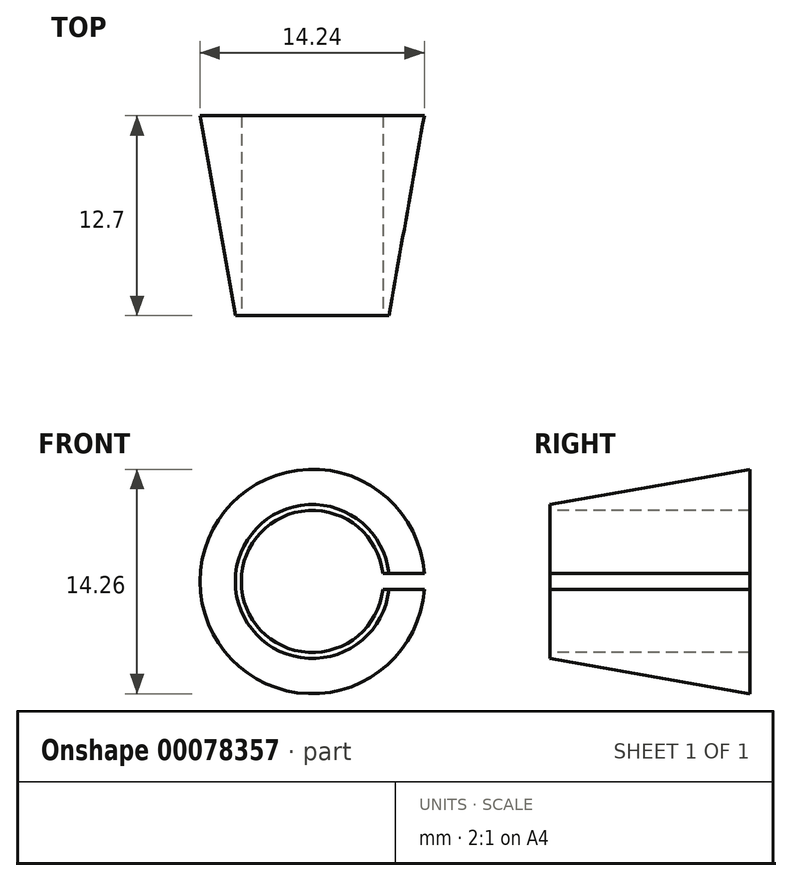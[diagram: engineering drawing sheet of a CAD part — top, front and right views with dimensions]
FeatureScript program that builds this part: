
annotation { "Feature Type Name" : "Feature", "Feature Type Description" : "" }
export const myFeature = defineFeature(function(context is Context, id is Id, definition is map)
    precondition{}
    {
        {
            var Q0;
            Q0=qCreatedBy(makeId("Right.planeOp"),FACE);
            var sketch = newSketch(context, id + "F0", { "sketchPlane" : qUnion([Q0])});
            skLineSegment(sketch, "E0", {"start": v(0, 4.89) * mm, "end": v(12.7, 7.13) * mm});
            skLineSegment(sketch, "E1", {"start": v(0, 0) * mm, "end": v(12.7, 0) * mm, "construction": true});
            skLineSegment(sketch, "E2", {"start": v(0, 4.5) * mm, "end": v(0, 4.89) * mm});
            skLineSegment(sketch, "E3", {"start": v(0, 4.5) * mm, "end": v(12.7, 4.5) * mm});
            skLineSegment(sketch, "E4", {"start": v(12.7, 7.13) * mm, "end": v(12.7, 4.5) * mm});
            skSolve(sketch);
        }
        {
            var Q0;
            Q0=makeQuery(id+"F0.imprint","IMPRINT",FACE,{"disambiguationData":[TD([[makeQuery(id+"F0.imprint","IMPRINT",EDGE,{"derivedFrom":sQuery(id+"F0.wireOp",EDGE,"E0")}),-1.0]])]});
            var Q1;
            Q1=sQuery(id+"F0.wireOp",EDGE,"E1");
            var Q2;
            Q2=sQuery(id+"F0.wireOp",EDGE,"E1");
            revolve(context, id + "F1", {"entities" : qUnion([Q0]), "surfaceEntities" : qUnion([Q1]), "axis" : qUnion([Q2]), "revolveType" : RevolveType.FULL});
        }
        {
            var Q0;
            Q0=qCreatedBy(makeId("Top.planeOp"),FACE);
            var sketch = newSketch(context, id + "F2", { "sketchPlane" : qUnion([Q0])});
            skLineSegment(sketch, "E5", {"start": v(1.85, 15.4) * mm, "end": v(1.85, 0) * mm});
            skLineSegment(sketch, "E6", {"start": v(1.85, 0) * mm, "end": v(15.35, 0) * mm});
            skLineSegment(sketch, "E7", {"start": v(15.35, 0) * mm, "end": v(15.35, 15.15) * mm});
            skLineSegment(sketch, "E8", {"start": v(15.35, 15.15) * mm, "end": v(1.85, 15.4) * mm});
            skSolve(sketch);
        }
        {
            var Q0;
            Q0 = qSketchRegion(id + "F2", true);
            extrude(context, id + "F3", {"entities" : qUnion([Q0]), "operationType" : NewBodyOperationType.REMOVE, "endBound" : BoundingType.SYMMETRIC, "depth" : 1.02 * mm});
        }
    });
